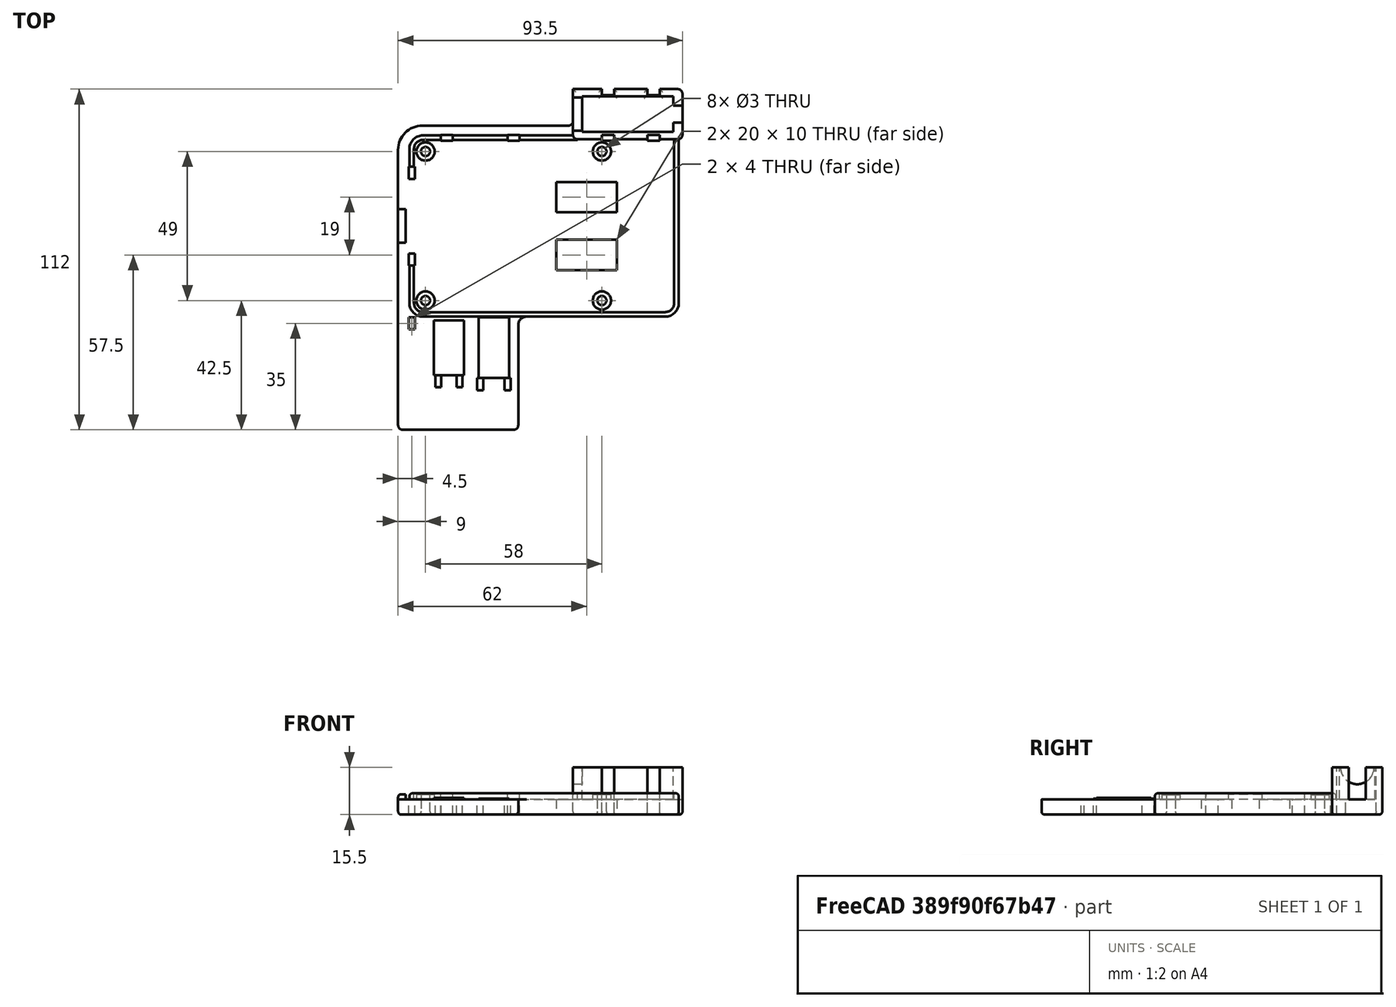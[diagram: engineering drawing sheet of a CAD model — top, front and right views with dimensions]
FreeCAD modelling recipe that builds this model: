
FCSTD DOCUMENT  (FreeCAD 0.18R4 (GitTag))
Label: raspberry_holster
License: All rights reserved
LicenseURL: http://en.wikipedia.org/wiki/All_rights_reserved
objects: Sketcher::SketchObject×10, PartDesign::Pad×7, PartDesign::Fillet×4, PartDesign::Pocket×3, Mesh::Feature×1, PartDesign::Body×1
note: 35 computed .brp shape members not serialized (recipe doc carries the construction recipe); baked Part::Feature solids carry a one-line shape summary decoded from their .brp

FEATURE [Mesh::Feature] Raspberry_Pi_4
  Placement = pos=(39,24.5,7.5) rot=(0,0,1;0rad)
FEATURE [Sketcher::SketchObject] Sketch  label="bottom_plane"
  MapMode = 5
  Support = -> [XY_Plane]
  sketch-geometry (71):
    g0: Circle CenterX=0 CenterY=49 CenterZ=0 NormalX=0 NormalY=0 NormalZ=1 AngleXU=0 Radius=1.5
    g1: Circle CenterX=58 CenterY=49 CenterZ=0 NormalX=0 NormalY=0 NormalZ=1 AngleXU=0 Radius=1.5
    g2: Circle CenterX=0 CenterY=0 CenterZ=0 NormalX=0 NormalY=0 NormalZ=1 AngleXU=0 Radius=1.5
    g3: Circle CenterX=58 CenterY=0 CenterZ=0 NormalX=0 NormalY=0 NormalZ=1 AngleXU=0 Radius=1.5
    g4: LineSegment StartX=84.5 StartY=68 StartZ=0 EndX=84.5 EndY=-5 EndZ=0
    g5: ArcOfCircle CenterX=83 CenterY=68 CenterZ=0 NormalX=0 NormalY=0 NormalZ=1 AngleXU=0 Radius=1.5 StartAngle=-9e-16 EndAngle=1.5708
    g6: LineSegment StartX=48.5 StartY=69.5 StartZ=0 EndX=48.5 EndY=59 EndZ=0
    g7: ArcOfCircle CenterX=47 CenterY=59 CenterZ=0 NormalX=0 NormalY=0 NormalZ=1 AngleXU=0 Radius=1.5 StartAngle=4.71239 EndAngle=6.28319
    g8: LineSegment StartX=47 StartY=57.5 StartZ=0 EndX=-1 EndY=57.5 EndZ=0
    g9: LineSegment StartX=-9 StartY=49.5 StartZ=0 EndX=-9 EndY=-41 EndZ=0
    g10: ArcOfCircle CenterX=-1 CenterY=49.5 CenterZ=0 NormalX=0 NormalY=0 NormalZ=1 AngleXU=0 Radius=8 StartAngle=1.5708 EndAngle=3.14159
    g11: LineSegment StartX=-7.5 StartY=-42.5 StartZ=0 EndX=29 EndY=-42.5 EndZ=0
    g12: ArcOfCircle CenterX=-7.5 CenterY=-41 CenterZ=0 NormalX=0 NormalY=0 NormalZ=1 AngleXU=0 Radius=1.5 StartAngle=3.14159 EndAngle=4.71239
    g13: ArcOfCircle CenterX=83 CenterY=-5 CenterZ=0 NormalX=0 NormalY=0 NormalZ=1 AngleXU=0 Radius=1.5 StartAngle=4.71239 EndAngle=6.28319
    g14: LineSegment StartX=32 StartY=-6.5 StartZ=0 EndX=83 EndY=-6.5 EndZ=0
    g15: LineSegment StartX=30.5 StartY=-8 StartZ=0 EndX=30.5 EndY=-41 EndZ=0
    g16: ArcOfCircle CenterX=32 CenterY=-8 CenterZ=0 NormalX=0 NormalY=0 NormalZ=1 AngleXU=0 Radius=1.5 StartAngle=1.5708 EndAngle=3.14159
    g17: ArcOfCircle CenterX=29 CenterY=-41 CenterZ=0 NormalX=0 NormalY=0 NormalZ=1 AngleXU=0 Radius=1.5 StartAngle=4.71239 EndAngle=6.28319
    g18: LineSegment StartX=58 StartY=52.5 StartZ=0 EndX=62 EndY=52.5 EndZ=0
    g19: LineSegment StartX=62 StartY=52.5 StartZ=0 EndX=62 EndY=54.5 EndZ=0
    g20: LineSegment StartX=62 StartY=54.5 StartZ=0 EndX=58 EndY=54.5 EndZ=0
    g21: LineSegment StartX=58 StartY=54.5 StartZ=0 EndX=58 EndY=52.5 EndZ=0
    g22: LineSegment StartX=73 StartY=54.5 StartZ=0 EndX=77 EndY=54.5 EndZ=0
    g23: LineSegment StartX=77 StartY=54.5 StartZ=0 EndX=77 EndY=52.5 EndZ=0
    g24: LineSegment StartX=77 StartY=52.5 StartZ=0 EndX=73 EndY=52.5 EndZ=0
    g25: LineSegment StartX=73 StartY=52.5 StartZ=0 EndX=73 EndY=54.5 EndZ=0
    g26: LineSegment StartX=48.5 StartY=69.5 StartZ=0 EndX=58 EndY=69.5 EndZ=0
    g27: LineSegment StartX=58 StartY=69.5 StartZ=0 EndX=58 EndY=67.5 EndZ=0
    g28: LineSegment StartX=58 StartY=67.5 StartZ=0 EndX=62 EndY=67.5 EndZ=0
    g29: LineSegment StartX=62 StartY=67.5 StartZ=0 EndX=62 EndY=69.5 EndZ=0
    g30: LineSegment StartX=62 StartY=69.5 StartZ=0 EndX=73 EndY=69.5 EndZ=0
    g31: LineSegment StartX=73 StartY=69.5 StartZ=0 EndX=73 EndY=67.5 EndZ=0
    g32: LineSegment StartX=73 StartY=67.5 StartZ=0 EndX=77 EndY=67.5 EndZ=0
    g33: LineSegment StartX=77 StartY=67.5 StartZ=0 EndX=77 EndY=69.5 EndZ=0
    g34: LineSegment StartX=77 StartY=69.5 StartZ=0 EndX=83 EndY=69.5 EndZ=0
    g35: LineSegment StartX=31 StartY=54.5 StartZ=0 EndX=27 EndY=54.5 EndZ=0
    g36: LineSegment StartX=27 StartY=54.5 StartZ=0 EndX=27 EndY=52.5 EndZ=0
    g37: LineSegment StartX=27 StartY=52.5 StartZ=0 EndX=31 EndY=52.5 EndZ=0
    g38: LineSegment StartX=31 StartY=52.5 StartZ=0 EndX=31 EndY=54.5 EndZ=0
    g39: LineSegment StartX=9 StartY=54.5 StartZ=0 EndX=5 EndY=54.5 EndZ=0
    g40: LineSegment StartX=5 StartY=54.5 StartZ=0 EndX=5 EndY=52.5 EndZ=0
    g41: LineSegment StartX=5 StartY=52.5 StartZ=0 EndX=9 EndY=52.5 EndZ=0
    g42: LineSegment StartX=9 StartY=52.5 StartZ=0 EndX=9 EndY=54.5 EndZ=0
    g43: LineSegment StartX=-5.5 StartY=44 StartZ=0 EndX=-3.5 EndY=44 EndZ=0
    g44: LineSegment StartX=-3.5 StartY=44 StartZ=0 EndX=-3.5 EndY=40 EndZ=0
    g45: LineSegment StartX=-3.5 StartY=40 StartZ=0 EndX=-5.5 EndY=40 EndZ=0
    g46: LineSegment StartX=-5.5 StartY=40 StartZ=0 EndX=-5.5 EndY=44 EndZ=0
    g47: LineSegment StartX=-5.5 StartY=15.5 StartZ=0 EndX=-3.5 EndY=15.5 EndZ=0
    g48: LineSegment StartX=-3.5 StartY=15.5 StartZ=0 EndX=-3.5 EndY=11.5 EndZ=0
    g49: LineSegment StartX=-3.5 StartY=11.5 StartZ=0 EndX=-5.5 EndY=11.5 EndZ=0
    g50: LineSegment StartX=-5.5 StartY=11.5 StartZ=0 EndX=-5.5 EndY=15.5 EndZ=0
    g51: LineSegment StartX=-5.5 StartY=-5.5 StartZ=0 EndX=-3.5 EndY=-5.5 EndZ=0
    g52: LineSegment StartX=-3.5 StartY=-5.5 StartZ=0 EndX=-3.5 EndY=-9.5 EndZ=0
    g53: LineSegment StartX=-3.5 StartY=-9.5 StartZ=0 EndX=-5.5 EndY=-9.5 EndZ=0
    g54: LineSegment StartX=-5.5 StartY=-9.5 StartZ=0 EndX=-5.5 EndY=-5.5 EndZ=0
    g55: LineSegment StartX=3.2 StartY=-24.5 StartZ=0 EndX=5.2 EndY=-24.5 EndZ=0
    g56: LineSegment StartX=5.2 StartY=-24.5 StartZ=0 EndX=5.2 EndY=-28.5 EndZ=0
    g57: LineSegment StartX=5.2 StartY=-28.5 StartZ=0 EndX=3.2 EndY=-28.5 EndZ=0
    g58: LineSegment StartX=3.2 StartY=-28.5 StartZ=0 EndX=3.2 EndY=-24.5 EndZ=0
    g59: LineSegment StartX=10.2 StartY=-24.5 StartZ=0 EndX=12.2 EndY=-24.5 EndZ=0
    g60: LineSegment StartX=12.2 StartY=-24.5 StartZ=0 EndX=12.2 EndY=-28.5 EndZ=0
    g61: LineSegment StartX=12.2 StartY=-28.5 StartZ=0 EndX=10.2 EndY=-28.5 EndZ=0
    g62: LineSegment StartX=10.2 StartY=-28.5 StartZ=0 EndX=10.2 EndY=-24.5 EndZ=0
    g63: LineSegment StartX=17 StartY=-25.5 StartZ=0 EndX=19 EndY=-25.5 EndZ=0
    g64: LineSegment StartX=19 StartY=-25.5 StartZ=0 EndX=19 EndY=-29.5 EndZ=0
    g65: LineSegment StartX=19 StartY=-29.5 StartZ=0 EndX=17 EndY=-29.5 EndZ=0
    g66: LineSegment StartX=17 StartY=-29.5 StartZ=0 EndX=17 EndY=-25.5 EndZ=0
    g67: LineSegment StartX=26 StartY=-25.5 StartZ=0 EndX=28 EndY=-25.5 EndZ=0
    g68: LineSegment StartX=28 StartY=-25.5 StartZ=0 EndX=28 EndY=-29.5 EndZ=0
    g69: LineSegment StartX=28 StartY=-29.5 StartZ=0 EndX=26 EndY=-29.5 EndZ=0
    g70: LineSegment StartX=26 StartY=-29.5 StartZ=0 EndX=26 EndY=-25.5 EndZ=0
  constraints (219):
    c: Coincident(g-1,g2)
    c: Vertical(g2,g0)
    c: Vertical(g1,g3)
    c: Horizontal(g1,g0)
    c: Horizontal(g3,g2)
    c: DistanceY(g2,g0) = 49
    c: DistanceX(g2,g3) = 58
    c: Radius(g2) = 1.5
    c: Equal(g2,g3)
    c: Equal(g3,g1)
    c: Equal(g1,g0)
    c: Vertical(g4)
    c: DistanceX(g3,g4) = 26.5
    c: Coincident(g5,g4)
    c: Vertical(g5,g5)
    c: Horizontal(g4,g5)
    c: Radius(g5) = 1.5
    c: Coincident(g6,g7)
    c: Vertical(g7,g7)
    c: Horizontal(g7,g6)
    c: Radius(g7) = 1.5
    c: Vertical(g6)
    c: DistanceX(g6,g4) = 36
    c: Coincident(g8,g7)
    c: Horizontal(g8)
    c: Vertical(g9)
    c: DistanceX(g9,g0) = 9
    c: DistanceY(g1,g7) = 8.5
    c: Coincident(g10,g8)
    c: Coincident(g9,g10)
    c: Vertical(g10,g8)
    c: Horizontal(g10,g9)
    c: Horizontal(g11)
    c: DistanceY(g11,g2) = 42.5
    c: Coincident(g11,g12)
    c: Coincident(g12,g9)
    c: Vertical(g12,g11)
    c: Horizontal(g9,g12)
    c: Radius(g12) = 1.5
    c: Coincident(g13,g4)
    c: Horizontal(g13,g4)
    c: Vertical(g13,g13)
    c: Radius(g13) = 1.5
    c: Coincident(g14,g13)
    c: Horizontal(g14)
    c: Coincident(g16,g14)
    c: Coincident(g16,g15)
    c: Vertical(g16,g14)
    c: Horizontal(g16,g15)
    c: DistanceY(g14,g3) = 6.5
    c: DistanceX(g2,g15) = 30.5
    c: Vertical(g15)
    c: Coincident(g17,g11)
    c: Coincident(g17,g15)
    c: Horizontal(g17,g15)
    c: Vertical(g11,g17)
    c: Radius(g17) = 1.5
    c: Radius(g16) = 1.5
    c: Coincident(g18,g19)
    c: Coincident(g19,g20)
    c: Coincident(g20,g21)
    c: Coincident(g21,g18)
    c: Horizontal(g18)
    c: Horizontal(g20)
    c: Vertical(g19)
    c: Vertical(g21)
    c: DistanceY(g18,g20) = 2
    c: DistanceX(g20,g19) = 4
    c: DistanceY(g1,g18) = 3.5
    c: Vertical(g1,g18)
    c: Coincident(g22,g23)
    c: Coincident(g23,g24)
    c: Coincident(g24,g25)
    c: Coincident(g25,g22)
    c: Horizontal(g22)
    c: Horizontal(g24)
    c: Vertical(g23)
    c: Vertical(g25)
    c: Horizontal(g22,g19)
    c: Horizontal(g24,g18)
    c: DistanceX(g22,g22) = 4
    c: DistanceX(g18,g24) = 15
    c: Coincident(g26,g27)
    c: Coincident(g27,g28)
    c: Coincident(g28,g29)
    c: Coincident(g29,g30)
    c: Coincident(g30,g31)
    c: Coincident(g31,g32)
    c: Coincident(g32,g33)
    c: Coincident(g33,g34)
    c: Coincident(g26,g6)
    c: Coincident(g34,g5)
    c: DistanceY(g1,g6) = 20.5
    c: Horizontal(g26)
    c: Horizontal(g30)
    c: Horizontal(g32)
    c: Horizontal(g34)
    c: Horizontal(g28)
    c: Vertical(g27)
    c: Vertical(g29)
    c: Vertical(g31)
    c: Vertical(g33)
    c: Horizontal(g26,g29)
    c: Horizontal(g30,g33)
    c: Horizontal(g31,g28)
    c: Vertical(g28,g19)
    c: Vertical(g20,g27)
    c: Vertical(g22,g31)
    c: Vertical(g22,g32)
    c: DistanceY(g28,g29) = 2
    c: Coincident(g35,g36)
    c: Coincident(g36,g37)
    c: Coincident(g38,g35)
    c: Horizontal(g35)
    c: Horizontal(g37)
    c: Vertical(g36)
    c: Vertical(g38)
    c: Coincident(g39,g40)
    c: Coincident(g40,g41)
    c: Coincident(g41,g42)
    c: Coincident(g42,g39)
    c: Horizontal(g39)
    c: Horizontal(g41)
    c: Vertical(g40)
    c: Vertical(g42)
    c: Coincident(g43,g44)
    c: Coincident(g44,g45)
    c: Coincident(g45,g46)
    c: Coincident(g46,g43)
    c: Horizontal(g43)
    c: Horizontal(g45)
    c: Vertical(g44)
    c: Vertical(g46)
    c: Coincident(g47,g48)
    c: Coincident(g48,g49)
    c: Coincident(g49,g50)
    c: Coincident(g50,g47)
    c: Horizontal(g47)
    c: Horizontal(g49)
    c: Vertical(g48)
    c: Vertical(g50)
    c: DistanceY(g1,g37) = 3.5
    c: DistanceX(g36,g37) = 4
    c: DistanceY(g37,g35) = 2
    c: DistanceX(g40,g41) = 4
    c: Horizontal(g41,g36)
    c: Horizontal(g39,g35)
    c: DistanceX(g37,g1) = 27
    c: DistanceX(g43,g0) = 3.5
    c: DistanceX(g43,g43) = 2
    c: DistanceY(g44,g43) = 4
    c: Vertical(g44,g47)
    c: Vertical(g47,g45)
    c: DistanceY(g49,g47) = 4
    c: DistanceY(g43,g0) = 5
    c: DistanceX(g0,g40) = 5
    c: DistanceY(g47,g44) = 24.5
    c: Coincident(g37,g38)
    c: Coincident(g51,g52)
    c: Coincident(g52,g53)
    c: Coincident(g53,g54)
    c: Coincident(g54,g51)
    c: Horizontal(g51)
    c: Horizontal(g53)
    c: Vertical(g52)
    c: Vertical(g54)
    c: Vertical(g51,g49)
    c: Vertical(g51,g48)
    c: DistanceY(g53,g51) = 4
    c: DistanceY(g51,g48) = 17
    c: Coincident(g55,g56)
    c: Coincident(g56,g57)
    c: Coincident(g57,g58)
    c: Coincident(g58,g55)
    c: Horizontal(g55)
    c: Horizontal(g57)
    c: Vertical(g56)
    c: Vertical(g58)
    c: Coincident(g59,g60)
    c: Coincident(g60,g61)
    c: Coincident(g61,g62)
    c: Coincident(g62,g59)
    c: Horizontal(g59)
    c: Horizontal(g61)
    c: Vertical(g60)
    c: Vertical(g62)
    c: Coincident(g63,g64)
    c: Coincident(g64,g65)
    c: Coincident(g65,g66)
    c: Coincident(g66,g63)
    c: Horizontal(g63)
    c: Horizontal(g65)
    c: Vertical(g64)
    c: Vertical(g66)
    c: Coincident(g67,g68)
    c: Coincident(g68,g69)
    c: Coincident(g69,g70)
    c: Coincident(g70,g67)
    c: Horizontal(g67)
    c: Horizontal(g69)
    c: Vertical(g68)
    c: Vertical(g70)
    c: DistanceX(g55,g55) = 2
    c: DistanceY(g56,g55) = 4
    c: Horizontal(g56,g61)
    c: Horizontal(g65,g69)
    c: Horizontal(g67,g63)
    c: Horizontal(g59,g55)
    c: DistanceX(g59,g59) = 2
    c: DistanceX(g63,g63) = 2
    c: DistanceX(g67,g67) = 2
    c: DistanceX(g56,g61) = 5
    c: DistanceX(g64,g69) = 7
    c: DistanceY(g65,g63) = 4
    c: DistanceY(g55,g2) = 24.5
    c: DistanceY(g63,g2) = 25.5
    c: DistanceX(g2,g55) = 5.2
    c: DistanceX(g2,g63) = 19
    c: Radius(g10) = 8
FEATURE [PartDesign::Pad] Pad  label="bottom_plane_pad"
  Length = 5
  Length2 = 100
  Profile = -> Sketch
  Type = 0
FEATURE [Sketcher::SketchObject] Sketch001  label="standoffs"
  ExternalGeometry = -> [Pad]
  MapMode = 5
  Placement = pos=(0,0,5) rot=(0,0,1;0rad)
  Support = -> [Pad]
  sketch-geometry (8):
    g0: Circle CenterX=0 CenterY=49 CenterZ=0 NormalX=0 NormalY=0 NormalZ=1 AngleXU=0 Radius=3
    g1: Circle CenterX=58 CenterY=49 CenterZ=0 NormalX=0 NormalY=0 NormalZ=1 AngleXU=0 Radius=3
    g2: Circle CenterX=58 CenterY=0 CenterZ=0 NormalX=0 NormalY=0 NormalZ=1 AngleXU=0 Radius=3
    g3: Circle CenterX=0 CenterY=0 CenterZ=0 NormalX=0 NormalY=0 NormalZ=1 AngleXU=0 Radius=3
    g4: Circle CenterX=58 CenterY=0 CenterZ=0 NormalX=0 NormalY=0 NormalZ=1 AngleXU=0 Radius=1.5
    g5: Circle CenterX=58 CenterY=49 CenterZ=0 NormalX=0 NormalY=0 NormalZ=1 AngleXU=0 Radius=1.5
    g6: Circle CenterX=0 CenterY=49 CenterZ=0 NormalX=0 NormalY=0 NormalZ=1 AngleXU=0 Radius=1.5
    g7: Circle CenterX=0 CenterY=0 CenterZ=0 NormalX=0 NormalY=0 NormalZ=1 AngleXU=0 Radius=1.5
  constraints (16):
    c: Coincident(g3,g-1)
    c: Coincident(g-5,g0)
    c: Coincident(g-6,g1)
    c: Coincident(g-3,g2)
    c: Equal(g2,g1)
    c: Equal(g1,g0)
    c: Equal(g0,g3)
    c: Radius(g1) = 3
    c: Coincident(g7,g3)
    c: Coincident(g2,g4)
    c: Coincident(g5,g1)
    c: Coincident(g6,g0)
    c: Equal(g5,g4)
    c: Equal(g4,g7)
    c: Equal(g7,g6)
    c: Equal(g6,g-5)
FEATURE [PartDesign::Pad] Pad001  label="standoffs_pad"
  BaseFeature = -> Pad
  Length = 1.5
  Length2 = 100
  Profile = -> Sketch001
  Type = 0
FEATURE [Sketcher::SketchObject] Sketch002  label="HDMI_holder"
  ExternalGeometry = -> [Pad001]
  MapMode = 5
  Placement = pos=(0,0,5) rot=(0,0,1;0rad)
  Support = -> [Pad001]
  sketch-geometry (31):
    g0: LineSegment StartX=84.5 StartY=54.5 StartZ=0 EndX=84.5 EndY=58.5 EndZ=0
    g1: LineSegment StartX=51.5 StartY=55.5 StartZ=0 EndX=81.5 EndY=55.5 EndZ=0
    g2: LineSegment StartX=81.5 StartY=55.5 StartZ=0 EndX=81.5 EndY=58.5 EndZ=0
    g3: LineSegment StartX=81.5 StartY=58.5 StartZ=0 EndX=84.5 EndY=58.5 EndZ=0
    g4: LineSegment StartX=51.5 StartY=55.5 StartZ=0 EndX=51.5 EndY=67.1 EndZ=0
    g5: LineSegment StartX=48.5 StartY=69.5 StartZ=0 EndX=48.5 EndY=54.5 EndZ=0
    g6: LineSegment StartX=51.5 StartY=67.1 StartZ=0 EndX=81.5 EndY=67.1 EndZ=0
    g7: LineSegment StartX=81.5 StartY=67.1 StartZ=0 EndX=81.5 EndY=64.1 EndZ=0
    g8: LineSegment StartX=81.5 StartY=64.1 StartZ=0 EndX=84.5 EndY=64.1 EndZ=0
    g9: LineSegment StartX=84.5 StartY=64.1 StartZ=0 EndX=84.5 EndY=68 EndZ=0
    g10: ArcOfCircle CenterX=83 CenterY=68 CenterZ=0 NormalX=0 NormalY=0 NormalZ=1 AngleXU=0 Radius=1.5 StartAngle=1.4e-15 EndAngle=1.5708
    g11: LineSegment StartX=83 StartY=69.5 StartZ=0 EndX=77 EndY=69.5 EndZ=0
    g12: LineSegment StartX=77 StartY=69.5 StartZ=0 EndX=77 EndY=67.5 EndZ=0
    g13: LineSegment StartX=77 StartY=67.5 StartZ=0 EndX=73 EndY=67.5 EndZ=0
    g14: LineSegment StartX=73 StartY=67.5 StartZ=0 EndX=73 EndY=69.5 EndZ=0
    g15: LineSegment StartX=73 StartY=69.5 StartZ=0 EndX=62 EndY=69.5 EndZ=0
    g16: LineSegment StartX=62 StartY=69.5 StartZ=0 EndX=62 EndY=67.5 EndZ=0
    g17: LineSegment StartX=62 StartY=67.5 StartZ=0 EndX=58 EndY=67.5 EndZ=0
    g18: LineSegment StartX=58 StartY=67.5 StartZ=0 EndX=58 EndY=69.5 EndZ=0
    g19: LineSegment StartX=58 StartY=69.5 StartZ=0 EndX=48.5 EndY=69.5 EndZ=0
    g20: ArcOfCircle CenterX=50 CenterY=54.5 CenterZ=0 NormalX=0 NormalY=0 NormalZ=1 AngleXU=0 Radius=1.5 StartAngle=3.14159 EndAngle=4.71239
    g21: LineSegment StartX=83 StartY=53 StartZ=0 EndX=77 EndY=53 EndZ=0
    g22: LineSegment StartX=77 StartY=53 StartZ=0 EndX=77 EndY=54.5 EndZ=0
    g23: LineSegment StartX=77 StartY=54.5 StartZ=0 EndX=73 EndY=54.5 EndZ=0
    g24: LineSegment StartX=73 StartY=54.5 StartZ=0 EndX=73 EndY=53 EndZ=0
    g25: LineSegment StartX=73 StartY=53 StartZ=0 EndX=62 EndY=53 EndZ=0
    g26: LineSegment StartX=62 StartY=53 StartZ=0 EndX=62 EndY=54.5 EndZ=0
    g27: LineSegment StartX=62 StartY=54.5 StartZ=0 EndX=58 EndY=54.5 EndZ=0
    g28: LineSegment StartX=58 StartY=54.5 StartZ=0 EndX=58 EndY=53 EndZ=0
    g29: LineSegment StartX=58 StartY=53 StartZ=0 EndX=50 EndY=53 EndZ=0
    g30: ArcOfCircle CenterX=83 CenterY=54.5 CenterZ=0 NormalX=0 NormalY=0 NormalZ=1 AngleXU=0 Radius=1.5 StartAngle=4.71239 EndAngle=6.28319
  constraints (84):
    c: Vertical(g0,g-6)
    c: Horizontal(g1)
    c: DistanceY(g20,g1) = 2.5
    c: Coincident(g0,g3)
    c: Coincident(g3,g2)
    c: Coincident(g2,g1)
    c: DistanceX(g2,g0) = 3
    c: Vertical(g0)
    c: Horizontal(g3)
    c: Vertical(g2)
    c: DistanceX(g1,g1) = 30
    c: DistanceY(g1,g2) = 3
    c: Coincident(g4,g6)
    c: Coincident(g1,g4)
    c: Coincident(g8,g9)
    c: Coincident(g7,g8)
    c: Coincident(g6,g7)
    c: Horizontal(g6)
    c: Vertical(g4)
    c: DistanceY(g1,g4) = 11.6
    c: Vertical(g7)
    c: Horizontal(g8)
    c: Vertical(g9)
    c: Vertical(g7,g2)
    c: DistanceY(g7,g6) = 3
    c: Coincident(g9,g-6)
    c: Coincident(g9,g10)
    c: Horizontal(g9,g10)
    c: Vertical(g10,g10)
    c: Radius(g10) = 1.5
    c: Coincident(g11,g12)
    c: Coincident(g12,g13)
    c: Coincident(g13,g14)
    c: Coincident(g14,g15)
    c: Coincident(g15,g16)
    c: Coincident(g16,g17)
    c: Coincident(g17,g18)
    c: Coincident(g18,g19)
    c: Coincident(g11,g10)
    c: Horizontal(g11)
    c: Vertical(g12)
    c: Coincident(g12,g-4)
    c: Coincident(g13,g-4)
    c: Coincident(g14,g-7)
    c: Coincident(g15,g-7)
    c: Coincident(g16,g-5)
    c: Coincident(g17,g-5)
    c: Coincident(g19,g-8)
    c: Horizontal(g19)
    c: Vertical(g18)
    c: Coincident(g5,g19)
    c: Coincident(g5,g20)
    c: Horizontal(g20,g5)
    c: Vertical(g20,g20)
    c: Radius(g20) = 1.5
    c: Vertical(g5)
    c: Coincident(g21,g22)
    c: Coincident(g22,g23)
    c: Coincident(g23,g24)
    c: Coincident(g24,g25)
    c: Coincident(g25,g26)
    c: Coincident(g26,g27)
    c: Coincident(g27,g28)
    c: Coincident(g28,g29)
    c: Coincident(g20,g29)
    c: Coincident(g27,g-12)
    c: Coincident(g26,g-11)
    c: Coincident(g23,g-10)
    c: Coincident(g22,g-9)
    c: Coincident(g30,g0)
    c: Coincident(g21,g30)
    c: Vertical(g30,g21)
    c: Horizontal(g30,g0)
    c: Radius(g30) = 1.5
    c: DistanceY(g-3,g28) = 4
    c: Horizontal(g29)
    c: Horizontal(g25)
    c: Horizontal(g21)
    c: Horizontal(g21,g24)
    c: Horizontal(g25,g28)
    c: Vertical(g28)
    c: Vertical(g26)
    c: Vertical(g24)
    c: Vertical(g22)
FEATURE [PartDesign::Pad] Pad002  label="HDMI_holder_pad"
  BaseFeature = -> Pad001
  Length = 10.5
  Length2 = 100
  Profile = -> Sketch002
  Type = 0
FEATURE [Sketcher::SketchObject] Sketch003  label="HDMI_wire_hole"
  ExternalGeometry = -> [Pad002]
  MapMode = 5
  Placement = pos=(48.5,0,0) rot=(0.57735,-0.57735,-0.57735;2.0944rad)
  Support = -> [Pad002]
  sketch-geometry (1):
    g0: Circle CenterX=-61.3 CenterY=15.5 CenterZ=0 NormalX=0 NormalY=0 NormalZ=1 AngleXU=0 Radius=5.5
  constraints (1):
    c: Radius(g0) = 5.5
FEATURE [PartDesign::Pocket] Pocket  label="Pocket_HDMI_wire_hole"
  BaseFeature = -> Pad002
  Length = 5
  Length2 = 100
  Profile = -> Sketch003
  Type = 0
FEATURE [Sketcher::SketchObject] Sketch004  label="SDcard_holder"
  ExternalGeometry = -> [Pocket]
  MapMode = 5
  Placement = pos=(0,0,5) rot=(0,0,1;0rad)
  Support = -> [Pocket]
  sketch-geometry (4):
    g0: LineSegment StartX=-9 StartY=30 StartZ=0 EndX=-6.5 EndY=30 EndZ=0
    g1: LineSegment StartX=-6.5 StartY=30 StartZ=0 EndX=-6.5 EndY=19 EndZ=0
    g2: LineSegment StartX=-6.5 StartY=19 StartZ=0 EndX=-9 EndY=19 EndZ=0
    g3: LineSegment StartX=-9 StartY=19 StartZ=0 EndX=-9 EndY=30 EndZ=0
  constraints (12):
    c: Coincident(g0,g1)
    c: Coincident(g1,g2)
    c: Coincident(g2,g3)
    c: Coincident(g3,g0)
    c: Horizontal(g0)
    c: Horizontal(g2)
    c: Vertical(g1)
    c: Vertical(g3)
    c: DistanceY(g-1,g1) = 19
    c: DistanceY(g0,g-4) = 19
    c: Vertical(g0,g-5)
    c: DistanceX(g1,g-1) = 6.5
FEATURE [PartDesign::Pad] Pad003  label="SDcard_holder_pad"
  BaseFeature = -> Pocket
  Length = 1.7
  Length2 = 100
  Profile = -> Sketch004
  Type = 0
FEATURE [Sketcher::SketchObject] Sketch005  label="typeC_support"
  ExternalGeometry = -> [Pad003]
  MapMode = 5
  Placement = pos=(0,0,5) rot=(0,0,1;0rad)
  Support = -> [Pad003]
  sketch-geometry (4):
    g0: LineSegment StartX=2.7 StartY=-6.5 StartZ=0 EndX=12.7 EndY=-6.5 EndZ=0
    g1: LineSegment StartX=12.7 StartY=-6.5 StartZ=0 EndX=12.7 EndY=-24.5 EndZ=0
    g2: LineSegment StartX=12.7 StartY=-24.5 StartZ=0 EndX=2.7 EndY=-24.5 EndZ=0
    g3: LineSegment StartX=2.7 StartY=-24.5 StartZ=0 EndX=2.7 EndY=-6.5 EndZ=0
  constraints (12):
    c: Coincident(g0,g1)
    c: Coincident(g1,g2)
    c: Coincident(g2,g3)
    c: Coincident(g3,g0)
    c: Horizontal(g0)
    c: Horizontal(g2)
    c: Vertical(g1)
    c: Vertical(g3)
    c: DistanceX(g0,g0) = 10
    c: DistanceY(g1,g1) = 18
    c: Horizontal(g2,g-4)
    c: DistanceX(g-1,g0) = 2.7
FEATURE [PartDesign::Pad] Pad004  label="typeC_support_pad"
  BaseFeature = -> Pad003
  Length = 0.5
  Length2 = 100
  Profile = -> Sketch005
  Type = 0
FEATURE [Sketcher::SketchObject] Sketch006  label="microHDMI_support"
  ExternalGeometry = -> [Pad004]
  MapMode = 5
  Placement = pos=(0,0,5) rot=(0,0,1;0rad)
  Support = -> [Pad004]
  sketch-geometry (4):
    g0: LineSegment StartX=17.5 StartY=-5.5 StartZ=0 EndX=27.5 EndY=-5.5 EndZ=0
    g1: LineSegment StartX=27.5 StartY=-5.5 StartZ=0 EndX=27.5 EndY=-25.5 EndZ=0
    g2: LineSegment StartX=27.5 StartY=-25.5 StartZ=0 EndX=17.5 EndY=-25.5 EndZ=0
    g3: LineSegment StartX=17.5 StartY=-25.5 StartZ=0 EndX=17.5 EndY=-5.5 EndZ=0
  constraints (12):
    c: Coincident(g0,g1)
    c: Coincident(g1,g2)
    c: Coincident(g2,g3)
    c: Coincident(g3,g0)
    c: Horizontal(g0)
    c: Horizontal(g2)
    c: Vertical(g1)
    c: Vertical(g3)
    c: DistanceX(g0,g0) = 10
    c: DistanceY(g1,g1) = 20
    c: Horizontal(g2,g-4)
    c: DistanceX(g-1,g0) = 17.5
FEATURE [PartDesign::Pad] Pad005  label="microHDMI_support_pad"
  BaseFeature = -> Pad004
  Length = 0.2
  Length2 = 100
  Profile = -> Sketch006
  Type = 0
FEATURE [Sketcher::SketchObject] Sketch007  label="dust_cover"
  ExternalGeometry = -> [Pad005]
  MapMode = 5
  Placement = pos=(0,0,5) rot=(0,0,1;0rad)
  Support = -> [Pad005]
  sketch-geometry (30):
    g0: LineSegment StartX=81.8 StartY=53 StartZ=0 EndX=81.8 EndY=-0.8 EndZ=0
    g1: LineSegment StartX=78.8 StartY=-3.8 StartZ=0 EndX=-0.8 EndY=-3.8 EndZ=0
    g2: LineSegment StartX=-3.8 StartY=49.8 StartZ=0 EndX=-3.8 EndY=44 EndZ=0
    g3: LineSegment StartX=-3.8 StartY=11.5 StartZ=0 EndX=-3.8 EndY=-0.8 EndZ=0
    g4: LineSegment StartX=-3.8 StartY=11.5 StartZ=0 EndX=-5.3 EndY=11.5 EndZ=0
    g5: ArcOfCircle CenterX=-0.8 CenterY=-0.8 CenterZ=0 NormalX=0 NormalY=0 NormalZ=1 AngleXU=0 Radius=3 StartAngle=3.14159 EndAngle=4.71239
    g6: ArcOfCircle CenterX=78.8 CenterY=-0.8 CenterZ=0 NormalX=0 NormalY=0 NormalZ=1 AngleXU=0 Radius=3 StartAngle=4.71239 EndAngle=6.28319
    g7: LineSegment StartX=81.8 StartY=53 StartZ=0 EndX=83 EndY=53 EndZ=0
    g8: LineSegment StartX=83.3 StartY=53.0303 StartZ=0 EndX=83.3 EndY=-0.8 EndZ=0
    g9: ArcOfCircle CenterX=83 CenterY=54.5 CenterZ=0 NormalX=0 NormalY=0 NormalZ=1 AngleXU=0 Radius=1.5 StartAngle=4.71239 EndAngle=4.91375
    g10: ArcOfCircle CenterX=78.8 CenterY=-0.8 CenterZ=0 NormalX=0 NormalY=0 NormalZ=1 AngleXU=0 Radius=4.5 StartAngle=4.71239 EndAngle=6.28319
    g11: LineSegment StartX=-0.8 StartY=-5.3 StartZ=0 EndX=78.8 EndY=-5.3 EndZ=0
    g12: ArcOfCircle CenterX=-0.8 CenterY=-0.8 CenterZ=0 NormalX=0 NormalY=0 NormalZ=1 AngleXU=0 Radius=4.5 StartAngle=3.14159 EndAngle=4.71239
    g13: LineSegment StartX=-5.3 StartY=-0.8 StartZ=0 EndX=-5.3 EndY=11.5 EndZ=0
    g14: LineSegment StartX=5 StartY=54.3 StartZ=0 EndX=5 EndY=52.8 EndZ=0
    g15: LineSegment StartX=5 StartY=54.3 StartZ=0 EndX=-0.8 EndY=54.3 EndZ=0
    g16: ArcOfCircle CenterX=-0.8 CenterY=49.8 CenterZ=0 NormalX=0 NormalY=0 NormalZ=1 AngleXU=0 Radius=4.5 StartAngle=1.5708 EndAngle=3.14159
    g17: LineSegment StartX=-3.8 StartY=44 StartZ=0 EndX=-5.3 EndY=44 EndZ=0
    g18: LineSegment StartX=-5.3 StartY=49.8 StartZ=0 EndX=-5.3 EndY=44 EndZ=0
    g19: LineSegment StartX=9 StartY=54.3 StartZ=0 EndX=27 EndY=54.3 EndZ=0
    g20: LineSegment StartX=27 StartY=54.3 StartZ=0 EndX=27 EndY=52.8 EndZ=0
    g21: LineSegment StartX=27 StartY=52.8 StartZ=0 EndX=9 EndY=52.8 EndZ=0
    g22: LineSegment StartX=9 StartY=52.8 StartZ=0 EndX=9 EndY=54.3 EndZ=0
    g23: LineSegment StartX=31 StartY=54.3 StartZ=0 EndX=31 EndY=52.8 EndZ=0
    g24: LineSegment StartX=31 StartY=52.8 StartZ=0 EndX=50 EndY=52.8 EndZ=0
    g25: LineSegment StartX=31 StartY=54.3 StartZ=0 EndX=48.5134 EndY=54.3 EndZ=0
    g26: LineSegment StartX=-0.8 StartY=52.8 StartZ=0 EndX=5 EndY=52.8 EndZ=0
    g27: LineSegment StartX=50 StartY=53 StartZ=0 EndX=50 EndY=52.8 EndZ=0
    g28: ArcOfCircle CenterX=50 CenterY=54.5 CenterZ=0 NormalX=0 NormalY=0 NormalZ=1 AngleXU=0 Radius=1.5 StartAngle=3.27532 EndAngle=4.71239
    g29: ArcOfCircle CenterX=-0.8 CenterY=49.8 CenterZ=0 NormalX=0 NormalY=0 NormalZ=1 AngleXU=0 Radius=3 StartAngle=1.5708 EndAngle=3.14159
  constraints (91):
    c: Vertical(g0)
    c: Horizontal(g1)
    c: Vertical(g3)
    c: Vertical(g2)
    c: DistanceX(g-3,g0) = 23.8
    c: DistanceY(g1,g-6) = 3.8
    c: Coincident(g4,g3)
    c: Horizontal(g3,g-7)
    c: Coincident(g5,g3)
    c: Coincident(g5,g1)
    c: Coincident(g6,g0)
    c: Coincident(g6,g1)
    c: Coincident(g7,g0)
    c: Horizontal(g7)
    c: Coincident(g7,g9)
    c: Coincident(g7,g-8)
    c: Vertical(g8)
    c: Coincident(g10,g8)
    c: Coincident(g10,g6)
    c: Coincident(g11,g10)
    c: Horizontal(g11)
    c: Coincident(g11,g12)
    c: Coincident(g12,g5)
    c: Coincident(g9,g-8)
    c: Coincident(g8,g9)
    c: DistanceX(g0,g8) = 1.5
    c: Coincident(g4,g13)
    c: Coincident(g12,g13)
    c: Vertical(g13)
    c: Horizontal(g4)
    c: Vertical(g14,g-9)
    c: Coincident(g14,g15)
    c: Vertical(g14)
    c: Horizontal(g15)
    c: Coincident(g15,g16)
    c: DistanceY(g26,g15) = 1.5
    c: Horizontal(g2,g-10)
    c: Coincident(g17,g2)
    c: Coincident(g17,g18)
    c: Coincident(g18,g16)
    c: Vertical(g18)
    c: Horizontal(g17)
    c: Coincident(g19,g20)
    c: Coincident(g20,g21)
    c: Coincident(g21,g22)
    c: Coincident(g22,g19)
    c: Horizontal(g19)
    c: Horizontal(g21)
    c: Vertical(g20)
    c: Vertical(g22)
    c: Vertical(g21,g-9)
    c: Vertical(g20,g-11)
    c: Horizontal(g21,g14)
    c: Horizontal(g19,g14)
    c: Coincident(g23,g24)
    c: Coincident(g23,g25)
    c: Vertical(g23)
    c: Vertical(g23,g-11)
    c: Horizontal(g23,g20)
    c: Horizontal(g23,g19)
    c: Horizontal(g24)
    c: Horizontal(g25)
    c: Coincident(g14,g26)
    c: Horizontal(g26)
    c: Coincident(g24,g27)
    c: Coincident(g27,g-12)
    c: Vertical(g27)
    c: Coincident(g25,g28)
    c: Coincident(g28,g27)
    c: Coincident(g28,g-12)
    c: Radius(g6) = 3
    c: Vertical(g10,g1)
    c: Vertical(g1,g6)
    c: Horizontal(g0,g6)
    c: Horizontal(g6,g8)
    c: Radius(g5) = 3
    c: Horizontal(g5,g3)
    c: Horizontal(g3,g12)
    c: Vertical(g11,g1)
    c: Vertical(g1,g5)
    c: DistanceX(g3,g-1) = 3.8
    c: Vertical(g26,g15)
    c: Horizontal(g2,g16)
    c: Coincident(g29,g26)
    c: Coincident(g29,g2)
    c: Coincident(g16,g29)
    c: Radius(g29) = 3
    c: Horizontal(g16,g2)
    c: Vertical(g16,g26)
    c: DistanceY(g-4,g26) = 3.8
    c: DistanceX(g2,g-4) = 3.8
FEATURE [PartDesign::Pad] Pad006  label="dust_cover_pad"
  BaseFeature = -> Pad005
  Length = 2
  Length2 = 100
  Profile = -> Sketch007
  Type = 0
FEATURE [Sketcher::SketchObject] Sketch008  label="top edge trim"
  ExternalGeometry = -> [Pad006]
  MapMode = 5
  Placement = pos=(0,0,5) rot=(0,0,1;0rad)
  Support = -> [Pad006]
  sketch-geometry (7):
    g0: ArcOfCircle CenterX=83 CenterY=54.5 CenterZ=0 NormalX=0 NormalY=0 NormalZ=1 AngleXU=0 Radius=1.5 StartAngle=4.91375 EndAngle=6.28319
    g1: LineSegment StartX=84.5 StartY=54.5 StartZ=0 EndX=84.5 EndY=-8 EndZ=0
    g2: LineSegment StartX=84.5 StartY=-8 StartZ=0 EndX=30.5 EndY=-8 EndZ=0
    g3: ArcOfCircle CenterX=33.2 CenterY=-8 CenterZ=0 NormalX=0 NormalY=0 NormalZ=1 AngleXU=0 Radius=2.7 StartAngle=1.5708 EndAngle=3.14159
    g4: LineSegment StartX=33.2 StartY=-5.3 StartZ=0 EndX=78.8 EndY=-5.3 EndZ=0
    g5: ArcOfCircle CenterX=78.8 CenterY=-0.8 CenterZ=0 NormalX=0 NormalY=0 NormalZ=1 AngleXU=0 Radius=4.5 StartAngle=4.71239 EndAngle=6.28319
    g6: LineSegment StartX=83.3 StartY=-0.8 StartZ=0 EndX=83.3 EndY=53.0303 EndZ=0
  constraints (19):
    c: Coincident(g0,g-7)
    c: Coincident(g0,g-3)
    c: Horizontal(g0,g0)
    c: Vertical(g1)
    c: Horizontal(g2)
    c: Coincident(g2,g1)
    c: Coincident(g1,g0)
    c: Coincident(g2,g-6)
    c: Coincident(g3,g2)
    c: Horizontal(g2,g3)
    c: Vertical(g3,g3)
    c: Horizontal(g3,g-5)
    c: Coincident(g4,g3)
    c: Coincident(g4,g-5)
    c: Coincident(g5,g4)
    c: Coincident(g5,g-4)
    c: Vertical(g4,g5)
    c: Coincident(g6,g5)
    c: Coincident(g6,g0)
FEATURE [PartDesign::Pocket] Pocket001  label="top edge trim pocket"
  BaseFeature = -> Pad006
  Length = 5
  Length2 = 100
  Profile = -> Sketch008
  Type = 0
FEATURE [Sketcher::SketchObject] Sketch009  label="belt clip guide"
  ExternalGeometry = -> [Pocket001]
  MapMode = 5
  Placement = pos=(0,0,5) rot=(0,0,1;0rad)
  Support = -> [Pocket001]
  sketch-geometry (8):
    g0: LineSegment StartX=63 StartY=39 StartZ=0 EndX=43 EndY=39 EndZ=0
    g1: LineSegment StartX=43 StartY=39 StartZ=0 EndX=43 EndY=29 EndZ=0
    g2: LineSegment StartX=43 StartY=29 StartZ=0 EndX=63 EndY=29 EndZ=0
    g3: LineSegment StartX=63 StartY=29 StartZ=0 EndX=63 EndY=39 EndZ=0
    g4: LineSegment StartX=63 StartY=20 StartZ=0 EndX=43 EndY=20 EndZ=0
    g5: LineSegment StartX=43 StartY=20 StartZ=0 EndX=43 EndY=10 EndZ=0
    g6: LineSegment StartX=43 StartY=10 StartZ=0 EndX=63 EndY=10 EndZ=0
    g7: LineSegment StartX=63 StartY=10 StartZ=0 EndX=63 EndY=20 EndZ=0
  constraints (24):
    c: Coincident(g0,g1)
    c: Coincident(g1,g2)
    c: Coincident(g2,g3)
    c: Coincident(g3,g0)
    c: Horizontal(g0)
    c: Horizontal(g2)
    c: Vertical(g1)
    c: Vertical(g3)
    c: Coincident(g4,g5)
    c: Coincident(g5,g6)
    c: Coincident(g6,g7)
    c: Coincident(g7,g4)
    c: Horizontal(g4)
    c: Horizontal(g6)
    c: Vertical(g5)
    c: Vertical(g7)
    c: Vertical(g4,g1)
    c: Vertical(g4,g2)
    c: DistanceY(g6,g4) = 10
    c: DistanceY(g2,g0) = 10
    c: DistanceX(g-3,g0) = 5
    c: DistanceX(g5,g6) = 20
    c: DistanceY(g-4,g6) = 10
    c: DistanceY(g0,g-3) = 10
FEATURE [PartDesign::Pocket] Pocket002  label="belt clip guide pocket"
  BaseFeature = -> Pocket001
  Length = 5
  Length2 = 100
  Profile = -> Sketch009
  Type = 0
FEATURE [PartDesign::Fillet] Fillet  label="underside fillet"
  Base = -> Pocket002 [Edge12,Edge3,Edge9,Edge13,Edge15,Edge17,Edge21,Edge19,Edge25,Edge23]
  BaseFeature = -> Pocket002
  Radius = 1
FEATURE [PartDesign::Fillet] Fillet001  label="SDcard fillet"
  Base = -> Fillet [Edge530]
  BaseFeature = -> Fillet
  Radius = 1
FEATURE [PartDesign::Fillet] Fillet002  label="dust cover fillet"
  Base = -> Fillet001 [Edge184,Edge178,Edge152,Edge138]
  BaseFeature = -> Fillet001
  Radius = 1
FEATURE [PartDesign::Fillet] Fillet003  label="mounting hole fillets"
  Base = -> Fillet002 [Edge434,Edge431,Edge432,Edge435]
  BaseFeature = -> Fillet002
  Radius = 1
FEATURE [PartDesign::Body] Body  label="raspberry holster v1.0"
  Group = -> [Sketch,Pad,Sketch001,Pad001,Sketch002,Pad002,Sketch003,Pocket,Sketch004,Pad003,Sketch005,Pad004,Sketch006,Pad005,Sketch007,Pad006,Sketch008,Pocket001,Sketch009,Pocket002,Fillet,Fillet001,Fillet002,Fillet003]
  Origin = -> Origin
  Tip = -> Fillet003
